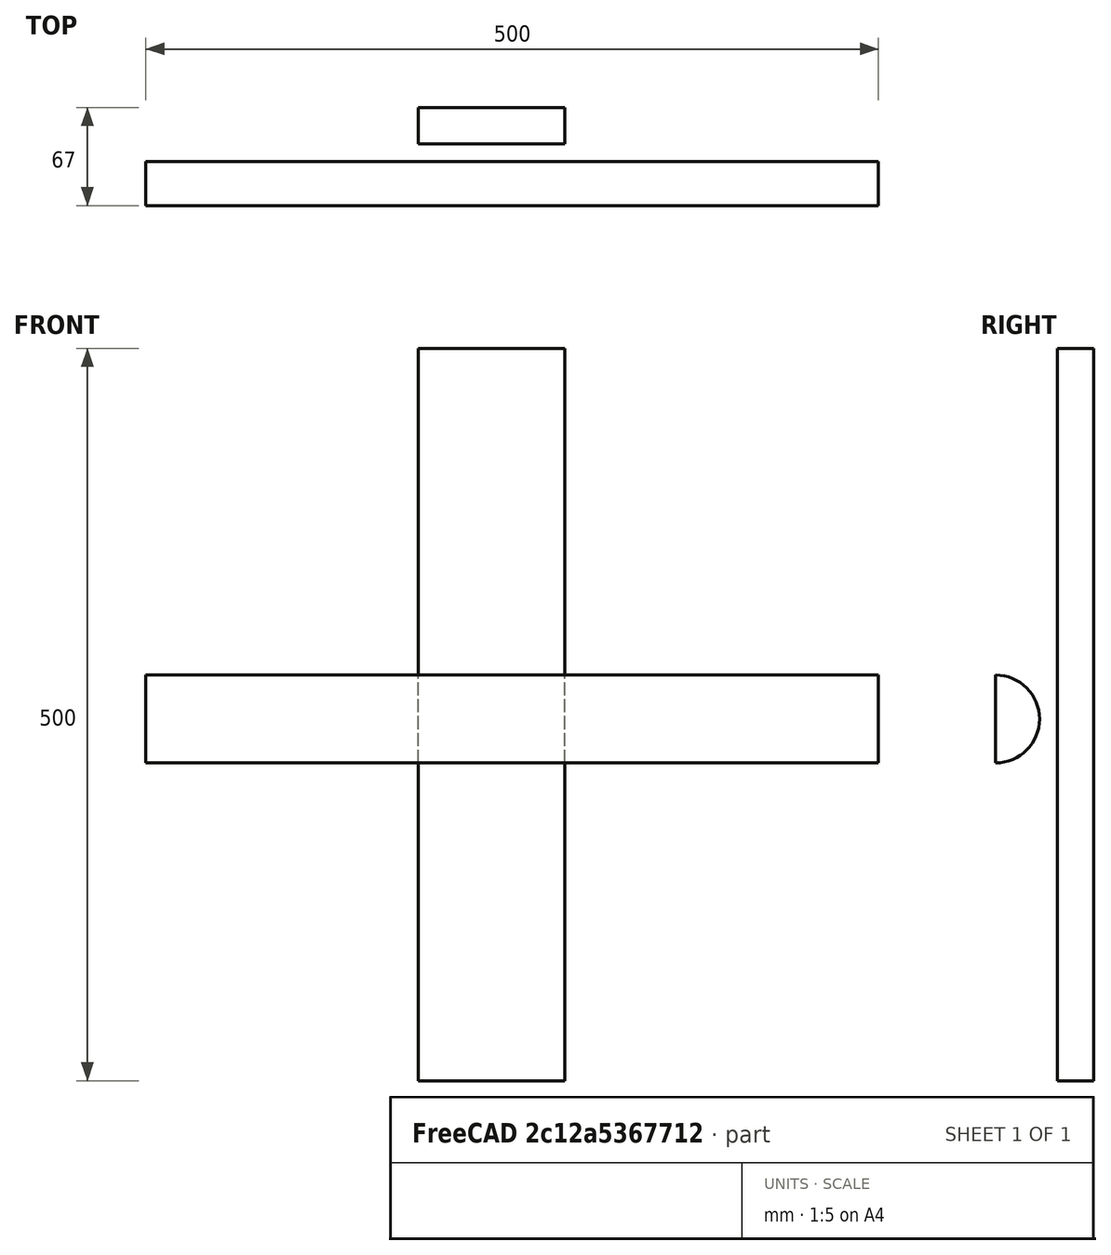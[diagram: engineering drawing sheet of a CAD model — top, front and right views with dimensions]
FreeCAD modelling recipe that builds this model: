
FCSTD DOCUMENT  (FreeCAD 0.19R19442 (Git))
Label: FEM_ccx_constraint_contact_solid_solidconstraint_contact_solid_solid
License: All rights reserved
LicenseURL: http://en.wikipedia.org/wiki/All_rights_reserved
objects: Part::Box×2, Part::Cylinder×1, Part::Cut×1, Part::MultiFuse×1, Fem::FemSolverObjectPython×1, App::MaterialObjectPython×1, Fem::ConstraintFixed×1, Fem::ConstraintPressure×1, Fem::ConstraintContact×1, Fem::FemMeshObject×1, Fem::FemAnalysis×1
note: 5 computed .brp shape members not serialized (recipe doc carries the construction recipe); baked Part::Feature solids carry a one-line shape summary decoded from their .brp

FEATURE [Part::Box] TopBox
  AttacherType = Attacher::AttachEngine3D
  Height = 500
  Length = 100
  Placement = pos=(186,0,-247) rot=(0,0,1;0rad)
  Width = 25
FEATURE [Part::Cylinder] BottomCylinder
  Angle = 360
  AttacherType = Attacher::AttachEngine3D
  Height = 500
  Placement = pos=(0,-42,0) rot=(0,1,0;1.5708rad)
  Radius = 30
FEATURE [Part::Box] BottomBox
  AttacherType = Attacher::AttachEngine3D
  Height = 100
  Length = 600
  Placement = pos=(-10,-142,-52) rot=(0,0,1;0rad)
  Width = 100
FEATURE [Part::Cut] BottomHalfCylinder
  Base = -> BottomCylinder
  Refine = true
  Tool = -> BottomBox
FEATURE [Part::MultiFuse] AllGeomFusion
  Refine = true
  Shapes = -> [TopBox,BottomHalfCylinder]
FEATURE [Fem::FemSolverObjectPython] CalculiXccxTools  # FEM object (typed FeaturePython)
  AnalysisType = 0
  BeamShellResultOutput3D = false
  EigenmodeHighLimit = 0
  EigenmodeLowLimit = 0
  EigenmodesCount = 15
  GeometricalNonlinearity = 0
  IterationsControlParameterCutb = 0.25,0.5,0.75,0.85,,,1.5,
  IterationsControlParameterIter = 4,8,9,200,10,400,,200,,
  IterationsControlParameterTimeUse = false
  IterationsThermoMechMaximum = 2000
  IterationsUserDefinedIncrementations = false
  IterationsUserDefinedTimeStepLength = false
  MaterialNonlinearity = 0
  MatrixSolverType = 0
  SplitInputWriter = false
  ThermoMechSteadyState = false
  TimeEnd = 1
  TimeInitialStep = 1
FEATURE [App::MaterialObjectPython] MechanicalMaterial  # material (typed FeaturePython)
  Category = 0
  Material = Name=Steel-Generic; PoissonRatio=0.30; YoungsModulus=200000 MPa
FEATURE [Fem::ConstraintFixed] ConstraintFixed
  NormalDirection = (0,0,-1)
  Normals = (48) [(0,0,-1),(0,0,-1),(0,0,-1),(0,0,-1),(0,0,-1),(0,0,-1),(0,0,-1),(0,0,-1),(0,0,-1),(0,0,-1),(0,0,-1),(0,0,-1),(0,0,-1),(0,0,-1),(0,0,-1),(0,0,-1),+32 more]
  Points = (48) [(186,0,-247),(219.333,0,-247),(252.667,0,-247),(286,0,-247),(186,8.33333,-247),(219.333,8.33333,-247),(252.667,8.33333,-247),(286,8.33333,-247),+40 more]
  References = -> [AllGeomFusion]
  Scale = 6
FEATURE [Fem::ConstraintPressure] ConstraintPressure
  NormalDirection = (0,-1,0)
  Normals = (16) [(0,-1,0),(0,-1,0),(0,-1,0),(0,-1,0),(0,-1,0),(0,-1,0),(0,-1,0),(0,-1,0),(0,-1,0),(0,-1,0),(0,-1,0),(0,-1,0),(0,-1,0),(0,-1,0),(0,-1,0),(0,-1,0)]
  Points = (16) [(-7.10543e-15,-42,-30),(-7.10543e-15,-42,-10),(-7.10543e-15,-42,10),(-7.10543e-15,-42,30),(166.667,-42,-30),(166.667,-42,-10),(166.667,-42,10),+9 more]
  Pressure = 100
  References = -> [AllGeomFusion]
  Scale = 18
FEATURE [Fem::ConstraintContact] ConstraintContact
  Friction = 0
  NormalDirection = (0,1,-1e-16)
  Normals = (32) [(2.22045e-16,0,-1),(1.11022e-16,0.866025,-0.5),(-1.11022e-16,0.866025,0.5),(-2.22045e-16,1.22465e-16,1),(2.22045e-16,0,-1),+27 more]
  Points = (32) [(6.66134e-15,-42,-30),(3.33067e-15,-16.0192,-15),(-3.33067e-15,-16.0192,15),(-6.66134e-15,-42,30),(166.667,-42,-30),(166.667,-16.0192,-15),+26 more]
  References = -> [AllGeomFusion]
  Scale = 19
  Slope = 1000000
FEATURE [Fem::FemMeshObject] Mesh
FEATURE [Fem::FemAnalysis] Analysis
  Group = -> [CalculiXccxTools,MechanicalMaterial,ConstraintFixed,ConstraintPressure,ConstraintContact,Mesh]
